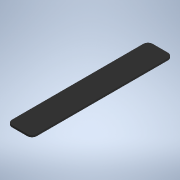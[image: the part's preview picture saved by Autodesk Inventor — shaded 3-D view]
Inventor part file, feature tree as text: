
AUTODESK INVENTOR PART (.ipt)
format: ipt  version: 2022 (Build 260153000, 153)  size: 111,104 bytes
history: native  units: mm
features: other x1, extrude x1, fillet x1, sketch x1
ambient origin geometry x8: Origin, YZ Plane, XZ Plane, XY Plane, X Axis, Y Axis, Z Axis, Center Point
bodies: Body1 (feature_tree)
feature tree (4):
  other  "Твердое тело1"
  extrude  "Выдавливание1"  Depth=9.0mm
  fillet  "Сопряжение1"  Radius=51.0mm
  sketch  "Эскиз1"
